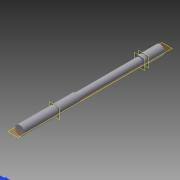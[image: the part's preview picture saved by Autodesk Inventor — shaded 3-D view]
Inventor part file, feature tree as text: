
AUTODESK INVENTOR PART (.ipt)
format: ipt  version: 2012 (Build 160160000, 160)  size: 99,840 bytes
history: native  units: in
note: dims shown in document units (in); Inventor stores cm internally (conversion verified against a paired STEP export)
features: extrude x4, sketch x4, plane x3
ambient origin geometry x8: Origin, YZ Plane, XZ Plane, XY Plane, X Axis, Y Axis, Z Axis, Center Point
bodies: Solid1 (feature_tree)
feature tree (11):
  extrude  "Extrusion1"  Depth=3.75in TaperAngle=0.0deg
  plane  "Work Plane5"
  extrude  "Extrusion4"  Depth=0.2in
  plane  "Work Plane6"
  extrude  "Extrusion5"  Depth=1.7in TaperAngle=0.0deg
  plane  "Work Plane7"
  extrude  "Extrusion6"  Depth=0.25in
  sketch  "Sketch1"  dims[d0=0.25in d1=3.75in d2=0.0in]
  sketch  "Sketch6"  dims[d10=-0.55in d11=0.2in]
  sketch  "Sketch7"  dims[d12=0.25in d13=1.7in d14=0.0in]
  sketch  "Sketch8"  dims[d15=0.11in d16=0.25in d17=0.23in d18=0.03in d19=0.0in d20=-2.28in d21=0.25in d22=0.23in d23=0.03in d24=0.0in]
